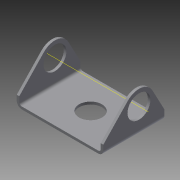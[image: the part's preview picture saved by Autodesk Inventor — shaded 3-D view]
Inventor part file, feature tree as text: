
AUTODESK INVENTOR PART (.ipt)
format: ipt  version: 2013 (Build 170138000, 138)  size: 198,144 bytes
history: native  units: in
note: dims shown in document units (in); Inventor stores cm internally (conversion verified against a paired STEP export)
features: other x8, sheet_metal_op x7, sketch x5
ambient origin geometry x8: Origin, YZ Plane, XZ Plane, XY Plane, X Axis, Y Axis, Z Axis, Center Point
bodies: Solid1 (feature_tree)
feature tree (20):
  sheet_metal_op  "Face1"
  sheet_metal_op  "Flange1"
  sheet_metal_op  "Flange2"
  other  "Work Axis1"
  sketch  "Sketch1"  dims[d0=4.0in]
  other  "Plate1"
  sketch  "Sketch2"  dims[d2=3.0in]
  other  "Plate2"
  sheet_metal_op  "Bend1"
  sheet_metal_op  "Corner1"
  sketch  "Sketch3"  dims[d3=0.125in]
  other  "Plate3"
  sheet_metal_op  "Bend2"
  sheet_metal_op  "Corner2"
  sketch  "Sketch4"  dims[d4=0.125in]
  sketch  "Sketch6"  dims[d5=0.0625in d6=0.25in d7=0.125in d8=2.0in d9=90.0deg d10=0.125in d11=0.5in d12=0.125in d13=0.125in d14=0.125in d15=0.0625in d16=0.25in d17=0.125in d18=2.0in d19=90.0deg d20=0.125in d21=0.5in d22=0.125in d23=0.125in d24=1.125in d25=0.75in d26=200.0in d27=0.0in d28=0.25in d29=0.25in d30=20.0in d31=0.0in d32=1.125in d33=0.125in d34=0.0in d35=1.5in d36=1.875in]
  other  "Cut1"
  other  "Cut2"
  other  "Cut3"
  other  "Definition1"
